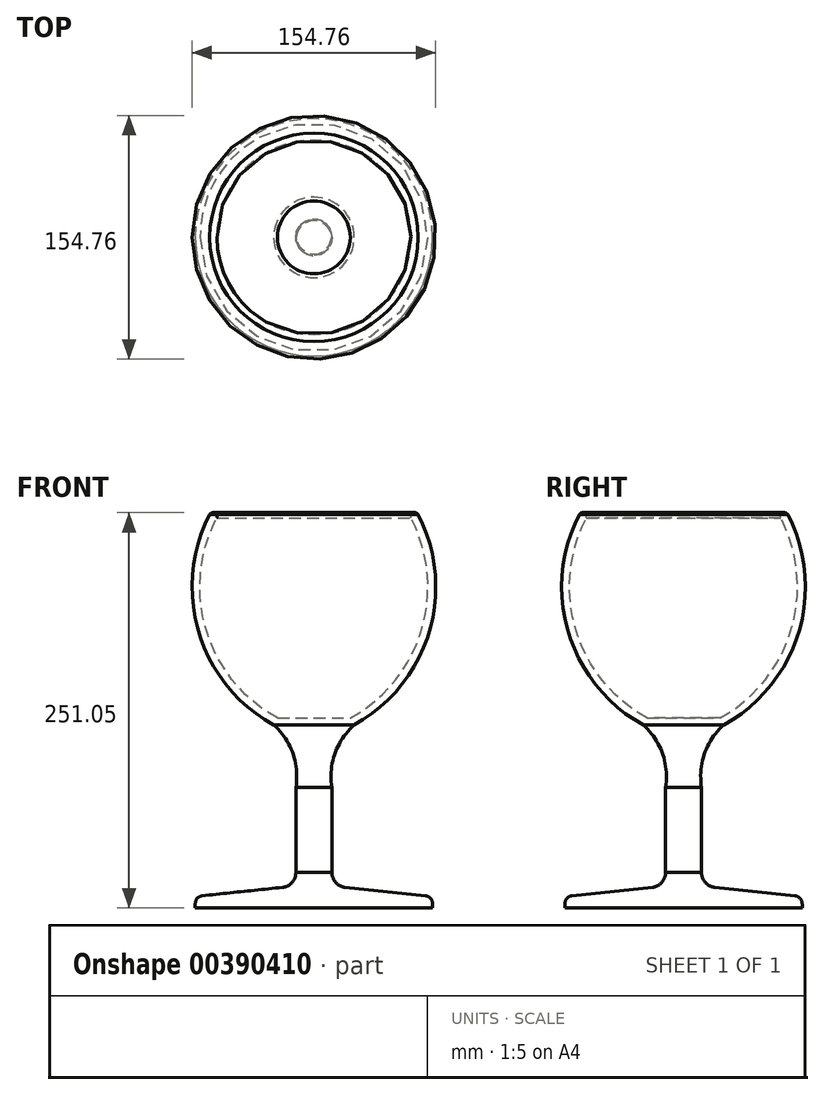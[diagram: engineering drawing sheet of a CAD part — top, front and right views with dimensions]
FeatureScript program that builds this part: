
annotation { "Feature Type Name" : "Feature", "Feature Type Description" : "" }
export const myFeature = defineFeature(function(context is Context, id is Id, definition is map)
    precondition{}
    {
        {
            var Q0;
            Q0=qCreatedBy(makeId("Front.planeOp"),FACE);
            var sketch = newSketch(context, id + "F0", { "sketchPlane" : qUnion([Q0])});
            skLineSegment(sketch, "E0", {"start": v(0, 0) * mm, "end": v(0, 250) * mm});
            skArc(sketch, "E1", {"start": v(-66.17, 250) * mm, "mid": v(-73.06, 174.84) * mm, "end": v(-25.54, 116.2) * mm});
            skArc(sketch, "E2", {"start": v(-11.46, 76.66) * mm, "mid": v(-13.4, 98.25) * mm, "end": v(-25.54, 116.2) * mm});
            skLineSegment(sketch, "E3", {"start": v(-11.46, 76.66) * mm, "end": v(-11.46, 22.5) * mm});
            skLineSegment(sketch, "E4", {"start": v(0, 0) * mm, "end": v(-75.37, 0) * mm});
            skLineSegment(sketch, "E5", {"start": v(-75.37, 7.23) * mm, "end": v(-19.8, 13.1) * mm});
            skLineSegment(sketch, "E6", {"start": v(-75.37, 0) * mm, "end": v(-75.37, 7.23) * mm});
            skArc(sketch, "E7", {"start": v(-19.8, 13.1) * mm, "mid": v(-13.82, 16.19) * mm, "end": v(-11.46, 22.5) * mm});
            skArc(sketch, "E8.0", {"start": v(-61.73, 247.7) * mm, "mid": v(-68.28, 176.3) * mm, "end": v(-23.13, 120.58) * mm});
            skLineSegment(sketch, "E9", {"start": v(-23.13, 120.58) * mm, "end": v(0, 120.58) * mm});
            skArc(sketch, "E10", {"start": v(-61.73, 247.7) * mm, "mid": v(-62.95, 250.77) * mm, "end": v(-66.17, 250) * mm});
            skSolve(sketch);
        }
        {
            var Q0;
            Q0=makeQuery(id+"F0.imprint","IMPRINT",FACE,{"disambiguationData":[TD([[makeQuery(id+"F0.imprint","IMPRINT",EDGE,{"derivedFrom":sQuery(id+"F0.wireOp",EDGE,"E1")}),1.0]])]});
            var Q1;
            Q1=sQuery(id+"F0.wireOp",EDGE,"E0");
            revolve(context, id + "F1", {"entities" : qUnion([Q0]), "axis" : qUnion([Q1]), "revolveType" : RevolveType.FULL});
        }
        {
            var Q0;
            Q0=makeQuery(id+"F1.opRevolve","SWEPT_EDGE",EDGE,{"disambiguationData":[OSD([sQuery(id+"F0.wireOp",EDGE,"E5"),sQuery(id+"F0.wireOp",EDGE,"E6")])]});
            fillet(context, id + "F2", {"entities" : qUnion([Q0]), "radius" : 5 * mm, "tangentPropagation" : true, "allowEdgeOverflow" : false});
        }
    });
